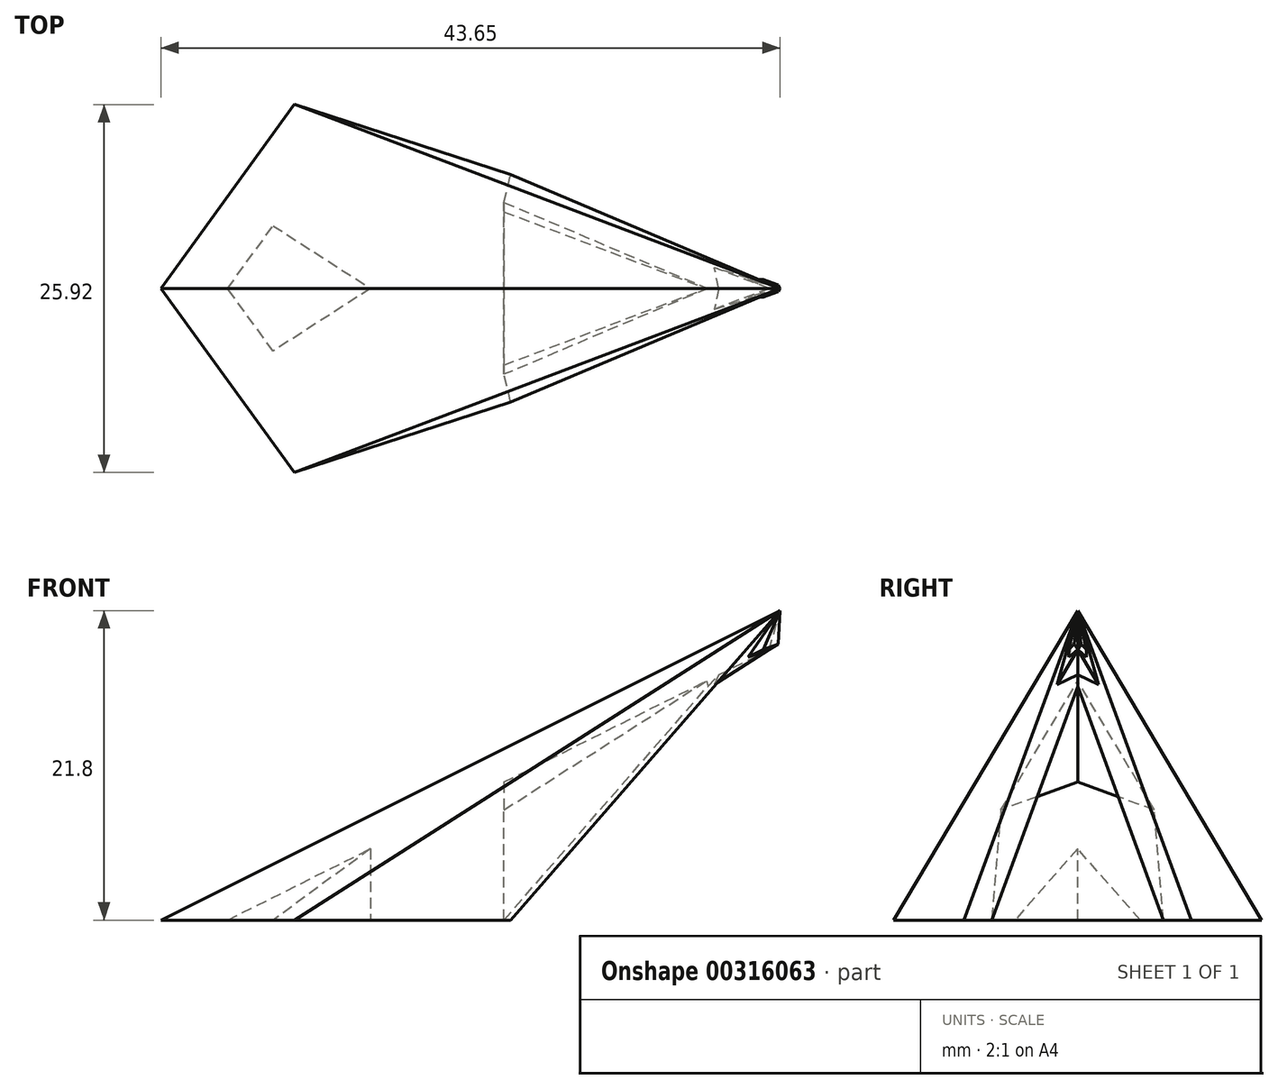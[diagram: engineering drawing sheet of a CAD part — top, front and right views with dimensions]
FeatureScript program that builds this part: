
annotation { "Feature Type Name" : "Feature", "Feature Type Description" : "" }
export const myFeature = defineFeature(function(context is Context, id is Id, definition is map)
    precondition{}
    {
        {
            var Q0;
            Q0=qCreatedBy(makeId("Top.planeOp"),FACE);
            var sketch = newSketch(context, id + "F0", { "sketchPlane" : qUnion([Q0])});
            skCircle(sketch, "E0.cCircle", {"center": v(0, 0) * mm, "radius": 11.03 * mm, "construction": true});
            skLineSegment(sketch, "E0.0", {"start": v(11.03, 8.01) * mm, "end": v(11.03, -8.01) * mm});
            skLineSegment(sketch, "E0.1", {"start": v(11.03, -8.01) * mm, "end": v(-4.21, -12.96) * mm});
            skLineSegment(sketch, "E0.2", {"start": v(-4.21, -12.96) * mm, "end": v(-13.63, 0) * mm});
            skLineSegment(sketch, "E0.3", {"start": v(-13.63, 0) * mm, "end": v(-4.21, 12.96) * mm});
            skLineSegment(sketch, "E0.4", {"start": v(-4.21, 12.96) * mm, "end": v(11.03, 8.01) * mm});
            skPoint(sketch, "E0.0.midPoint", {"position": v(11.03, 0) * mm});
            skSolve(sketch);
        }
        {
            var Q0;
            Q0=qCreatedBy(makeId("Front.planeOp"),FACE);
            var sketch = newSketch(context, id + "F1", { "sketchPlane" : qUnion([Q0])});
            skLineSegment(sketch, "E1", {"start": v(0, 0) * mm, "end": v(30.02, 21.8) * mm});
            skSolve(sketch);
        }
        {
            var Q0;
            Q0=sQuery(id+"F1.wireOp",VERTEX,"E1.end");
            var Q1;
            Q1=sQuery(id+"F0.wireOp",VERTEX,"E0.1.start");
            var Q2;
            Q2=sQuery(id+"F0.wireOp",VERTEX,"E0.2.start");
            cPlane(context, id + "F2", {"entities" : qUnion([Q0, Q1, Q2]), "cplaneType" : CPlaneType.THREE_POINT, "offset" : 25.4 * mm, "oppositeDirection" : true, "width" : 152.4 * mm, "height" : 152.4 * mm});
        }
        {
            var Q0;
            Q0=sQuery(id+"F0.wireOp",VERTEX,"E0.2.start");
            var Q1;
            Q1=sQuery(id+"F0.wireOp",VERTEX,"E0.3.start");
            var Q2;
            Q2=sQuery(id+"F1.wireOp",VERTEX,"E1.end");
            cPlane(context, id + "F3", {"entities" : qUnion([Q0, Q1, Q2]), "cplaneType" : CPlaneType.THREE_POINT, "offset" : 25.4 * mm, "width" : 152.4 * mm, "height" : 152.4 * mm});
        }
        {
            var Q0;
            Q0=sQuery(id+"F1.wireOp",VERTEX,"E1.end");
            var Q1;
            Q1=sQuery(id+"F0.wireOp",VERTEX,"E0.3.start");
            var Q2;
            Q2=sQuery(id+"F0.wireOp",VERTEX,"E0.4.start");
            cPlane(context, id + "F4", {"entities" : qUnion([Q0, Q1, Q2]), "cplaneType" : CPlaneType.THREE_POINT, "offset" : 25.4 * mm, "width" : 152.4 * mm, "height" : 152.4 * mm});
        }
        {
            var Q0;
            Q0=qCreatedBy(id+"F2.planeOp",FACE);
            var sketch = newSketch(context, id + "F5", { "sketchPlane" : qUnion([Q0])});
            skLineSegment(sketch, "E2", {"start": v(28, 21.72) * mm, "end": v(8.03, -0.67) * mm});
            skLineSegment(sketch, "E3", {"start": v(8.03, -0.67) * mm, "end": v(-7.99, -1.1) * mm});
            skLineSegment(sketch, "E4", {"start": v(-7.99, -1.1) * mm, "end": v(28, 21.72) * mm});
            skSolve(sketch);
        }
        {
            var Q0;
            Q0=qCreatedBy(id+"F3.planeOp",FACE);
            var sketch = newSketch(context, id + "F6", { "sketchPlane" : qUnion([Q0])});
            skLineSegment(sketch, "E5", {"start": v(35.88, 7.43) * mm, "end": v(-1.93, -12.19) * mm});
            skLineSegment(sketch, "E6", {"start": v(-1.93, -12.19) * mm, "end": v(-12.34, 0) * mm});
            skLineSegment(sketch, "E7", {"start": v(-12.34, 0) * mm, "end": v(35.88, 7.43) * mm});
            skSolve(sketch);
        }
        {
            var Q0;
            Q0=qCreatedBy(id+"F4.planeOp",FACE);
            var sketch = newSketch(context, id + "F7", { "sketchPlane" : qUnion([Q0])});
            skLineSegment(sketch, "E8", {"start": v(-1.93, 12.19) * mm, "end": v(-12.34, 0) * mm});
            skLineSegment(sketch, "E9", {"start": v(-12.34, 0) * mm, "end": v(35.88, -7.43) * mm});
            skLineSegment(sketch, "E10", {"start": v(35.88, -7.43) * mm, "end": v(-1.93, 12.19) * mm});
            skSolve(sketch);
        }
        {
            var Q0;
            Q0=sQuery(id+"F0.wireOp",VERTEX,"E0.4.end");
            var Q1;
            Q1=sQuery(id+"F5.wireOp",VERTEX,"E4.end");
            var Q2;
            Q2=sQuery(id+"F7.wireOp",VERTEX,"E10.end");
            cPlane(context, id + "F8", {"entities" : qUnion([Q0, Q1, Q2]), "cplaneType" : CPlaneType.THREE_POINT, "offset" : 25.4 * mm, "width" : 152.4 * mm, "height" : 152.4 * mm});
        }
        {
            var Q0;
            Q0=qCreatedBy(id+"F8.planeOp",FACE);
            var sketch = newSketch(context, id + "F9", { "sketchPlane" : qUnion([Q0])});
            skLineSegment(sketch, "E11", {"start": v(-28, 21.72) * mm, "end": v(7.99, -1.1) * mm});
            skLineSegment(sketch, "E12", {"start": v(7.99, -1.1) * mm, "end": v(-8.03, -0.67) * mm});
            skLineSegment(sketch, "E13", {"start": v(-8.03, -0.67) * mm, "end": v(-28, 21.72) * mm});
            skSolve(sketch);
        }
        {
            var Q0;
            Q0=makeQuery(id+"F9.imprint","IMPRINT",FACE,{"disambiguationData":[TD([[makeQuery(id+"F9.imprint","IMPRINT",EDGE,{"derivedFrom":sQuery(id+"F9.wireOp",EDGE,"E11")}),-1.0]])]});
            extrude(context, id + "F10", {"entities" : qUnion([Q0]), "oppositeDirection" : true, "depth" : 2 * mm});
        }
        {
            var Q0;
            Q0=makeQuery(id+"F7.imprint","IMPRINT",FACE,{"disambiguationData":[TD([[makeQuery(id+"F7.imprint","IMPRINT",EDGE,{"derivedFrom":sQuery(id+"F7.wireOp",EDGE,"E8")}),1.0]])]});
            extrude(context, id + "F11", {"entities" : qUnion([Q0]), "operationType" : NewBodyOperationType.ADD, "oppositeDirection" : true, "depth" : 2 * mm});
        }
        {
            var Q0;
            Q0=makeQuery(id+"F6.imprint","IMPRINT",FACE,{"disambiguationData":[TD([[makeQuery(id+"F6.imprint","IMPRINT",EDGE,{"derivedFrom":sQuery(id+"F6.wireOp",EDGE,"E5")}),-1.0]])]});
            extrude(context, id + "F12", {"entities" : qUnion([Q0]), "operationType" : NewBodyOperationType.ADD, "oppositeDirection" : true, "depth" : 2 * mm});
        }
        {
            var Q0;
            Q0=makeQuery(id+"F5.imprint","IMPRINT",FACE,{"disambiguationData":[TD([[makeQuery(id+"F5.imprint","IMPRINT",EDGE,{"derivedFrom":sQuery(id+"F5.wireOp",EDGE,"E2")}),-1.0]])]});
            extrude(context, id + "F13", {"entities" : qUnion([Q0]), "operationType" : NewBodyOperationType.ADD, "oppositeDirection" : true, "depth" : 2 * mm});
        }
        {
            var Q0;
            Q0=makeQuery(id+"F13.opExtrude","CAP_FACE",FACE,{"disambiguationData":[OSD([sQuery(id+"F5.wireOp",EDGE,"E2"),sQuery(id+"F5.wireOp",EDGE,"E3"),sQuery(id+"F5.wireOp",EDGE,"E4")])],"isStart":true});
            var sketch = newSketch(context, id + "F14", { "sketchPlane" : qUnion([Q0])});
            skLineSegment(sketch, "E14.bottom", {"start": v(21.55, 22.32) * mm, "end": v(30.03, 22.32) * mm});
            skLineSegment(sketch, "E14.top", {"start": v(21.55, 16.8) * mm, "end": v(30.03, 16.8) * mm});
            skLineSegment(sketch, "E14.left", {"start": v(21.55, 22.32) * mm, "end": v(21.55, 16.8) * mm});
            skLineSegment(sketch, "E14.right", {"start": v(30.03, 22.32) * mm, "end": v(30.03, 16.8) * mm});
            skSolve(sketch);
        }
        {
            var Q0;
            Q0=qSketchRegion(id+"F14",true);
            extrude(context, id + "F15", {"entities" : qUnion([Q0]), "operationType" : NewBodyOperationType.REMOVE, "depth" : 25.4 * mm});
        }
        {
            var Q0;
            Q0=makeQuery(id+"F11.opExtrude","CAP_FACE",FACE,{"disambiguationData":[OSD([sQuery(id+"F7.wireOp",EDGE,"E8"),sQuery(id+"F7.wireOp",EDGE,"E9"),sQuery(id+"F7.wireOp",EDGE,"E10")])],"isStart":true});
            var sketch = newSketch(context, id + "F16", { "sketchPlane" : qUnion([Q0])});
            skLineSegment(sketch, "E15.bottom", {"start": v(43.57, -4.34) * mm, "end": v(21.34, -4.34) * mm});
            skLineSegment(sketch, "E15.top", {"start": v(43.57, -8.99) * mm, "end": v(21.34, -8.99) * mm});
            skLineSegment(sketch, "E15.left", {"start": v(43.57, -4.34) * mm, "end": v(43.57, -8.99) * mm});
            skLineSegment(sketch, "E15.right", {"start": v(21.34, -4.34) * mm, "end": v(21.34, -8.99) * mm});
            skSolve(sketch);
        }
        {
            var Q0;
            Q0=qSketchRegion(id+"F16",true);
            extrude(context, id + "F17", {"entities" : qUnion([Q0]), "operationType" : NewBodyOperationType.REMOVE, "depth" : 25.4 * mm});
        }
        {
            var Q0;
            Q0=makeQuery(id+"F12.opExtrude","CAP_FACE",FACE,{"disambiguationData":[OSD([sQuery(id+"F6.wireOp",EDGE,"E5"),sQuery(id+"F6.wireOp",EDGE,"E6"),sQuery(id+"F6.wireOp",EDGE,"E7")])],"isStart":true});
            var sketch = newSketch(context, id + "F18", { "sketchPlane" : qUnion([Q0])});
            skLineSegment(sketch, "E16.bottom", {"start": v(31.54, 2.1) * mm, "end": v(39.49, 2.1) * mm});
            skLineSegment(sketch, "E16.top", {"start": v(31.54, 9.38) * mm, "end": v(39.49, 9.38) * mm});
            skLineSegment(sketch, "E16.left", {"start": v(31.54, 2.1) * mm, "end": v(31.54, 9.38) * mm});
            skLineSegment(sketch, "E16.right", {"start": v(39.49, 2.1) * mm, "end": v(39.49, 9.38) * mm});
            skSolve(sketch);
        }
        {
            var Q0;
            Q0=qSketchRegion(id+"F18",true);
            extrude(context, id + "F19", {"entities" : qUnion([Q0]), "operationType" : NewBodyOperationType.REMOVE, "depth" : 25.4 * mm});
        }
        {
            var Q0;
            Q0=makeQuery(id+"F10.opExtrude","CAP_FACE",FACE,{"disambiguationData":[OSD([sQuery(id+"F9.wireOp",EDGE,"E11"),sQuery(id+"F9.wireOp",EDGE,"E12"),sQuery(id+"F9.wireOp",EDGE,"E13")])],"isStart":true});
            var sketch = newSketch(context, id + "F20", { "sketchPlane" : qUnion([Q0])});
            skLineSegment(sketch, "E17.bottom", {"start": v(-23.79, 12.88) * mm, "end": v(-29.7, 12.88) * mm});
            skLineSegment(sketch, "E17.top", {"start": v(-23.79, 24.27) * mm, "end": v(-29.7, 24.27) * mm});
            skLineSegment(sketch, "E17.left", {"start": v(-23.79, 12.88) * mm, "end": v(-23.79, 24.27) * mm});
            skLineSegment(sketch, "E17.right", {"start": v(-29.7, 12.88) * mm, "end": v(-29.7, 24.27) * mm});
            skSolve(sketch);
        }
        {
            var Q0;
            Q0=qSketchRegion(id+"F20",true);
            extrude(context, id + "F21", {"entities" : qUnion([Q0]), "operationType" : NewBodyOperationType.REMOVE, "depth" : 25.4 * mm});
        }
        {
            var Q0;
            Q0=qSketchRegion(id+"F0",true);
            extrude(context, id + "F22", {"entities" : qUnion([Q0]), "operationType" : NewBodyOperationType.REMOVE, "oppositeDirection" : true, "depth" : 25.4 * mm});
        }
        {
            var Q0;
            Q0=makeQuery(id+"F22.boolean.opBoolean","COPY",FACE,{"derivedFrom":makeQuery(id+"F22.opExtrude","CAP_FACE",FACE,{"disambiguationData":[OSD([sQuery(id+"F0.wireOp",EDGE,"E0.0"),sQuery(id+"F0.wireOp",EDGE,"E0.1"),sQuery(id+"F0.wireOp",EDGE,"E0.2"),sQuery(id+"F0.wireOp",EDGE,"E0.3"),sQuery(id+"F0.wireOp",EDGE,"E0.4")])],"isStart":true})});
            var sketch = newSketch(context, id + "F23", { "sketchPlane" : qUnion([Q0])});
            skLineSegment(sketch, "E18", {"start": v(-8.92, 6.48) * mm, "end": v(10.55, -6.06) * mm});
            skLineSegment(sketch, "E19", {"start": v(10.55, 6.06) * mm, "end": v(-8.92, -6.48) * mm});
            skLineSegment(sketch, "E20", {"start": v(10.55, 6.06) * mm, "end": v(10.55, -6.06) * mm});
            skLineSegment(sketch, "E21", {"start": v(6.73, 7.3) * mm, "end": v(6.73, -7.3) * mm});
            skSolve(sketch);
        }
        {
            var Q0;
            {var subQ12=sQuery(id+"F23.wireOp",EDGE,"E19");var subQ16=sQuery(id+"F23.wireOp",EDGE,"E18");var subQ18=makeQuery(id+"F23.imprint","INTERSECT",VERTEX,{"derivedFrom":[subQ16,subQ12]});Q0=makeQuery(id+"F23.imprint","IMPRINT",FACE,{"disambiguationData":[TD([[makeQuery(id+"F23.imprint","IMPRINT",EDGE,{"disambiguationData":[TD([[subQ18,-1.0]])],"derivedFrom":subQ16}),-1.0]])]});}
            var Q1;
            {var subQ17=sQuery(id+"F23.wireOp",EDGE,"E19");var subQ24=sQuery(id+"F23.wireOp",EDGE,"E18");var subQ26=makeQuery(id+"F23.imprint","INTERSECT",VERTEX,{"derivedFrom":[subQ24,subQ17]});Q1=makeQuery(id+"F23.imprint","IMPRINT",FACE,{"disambiguationData":[TD([[makeQuery(id+"F23.imprint","IMPRINT",EDGE,{"disambiguationData":[TD([[subQ26,1.0]])],"derivedFrom":subQ17}),-1.0]])]});}
            var Q2;
            {var subQ0=sQuery(id+"F23.wireOp",EDGE,"E19");var subQ1=sQuery(id+"F23.wireOp",EDGE,"E18");var subQ2=makeQuery(id+"F23.imprint","INTERSECT",VERTEX,{"derivedFrom":[subQ1,subQ0]});Q2=makeQuery(id+"F23.imprint","IMPRINT",FACE,{"disambiguationData":[TD([[makeQuery(id+"F23.imprint","IMPRINT",EDGE,{"disambiguationData":[TD([[subQ2,-1.0]])],"derivedFrom":subQ1}),1.0]])]});}
            var Q3;
            {var subQ0=sQuery(id+"F23.wireOp",EDGE,"E19");var subQ23=sQuery(id+"F23.wireOp",EDGE,"E21");var subQ24=makeQuery(id+"F23.imprint","INTERSECT",VERTEX,{"derivedFrom":[subQ0,subQ23]});Q3=makeQuery(id+"F23.imprint","IMPRINT",FACE,{"disambiguationData":[TD([[makeQuery(id+"F23.imprint","IMPRINT",EDGE,{"disambiguationData":[TD([[subQ24,1.0]])],"derivedFrom":subQ23}),1.0]])]});}
            var Q4;
            {var subQ0=sQuery(id+"F23.wireOp",EDGE,"E20");Q4=makeQuery(id+"F23.imprint","IMPRINT",FACE,{"disambiguationData":[TD([[makeQuery(id+"F23.imprint","IMPRINT",EDGE,{"derivedFrom":subQ0}),-1.0]])]});}
            var Q5;
            {var subQ0=sQuery(id+"F23.wireOp",EDGE,"E18");var subQ14=sQuery(id+"F23.wireOp",EDGE,"E21");var subQ15=makeQuery(id+"F23.imprint","INTERSECT",VERTEX,{"derivedFrom":[subQ0,subQ14]});Q5=makeQuery(id+"F23.imprint","IMPRINT",FACE,{"disambiguationData":[TD([[makeQuery(id+"F23.imprint","IMPRINT",EDGE,{"disambiguationData":[TD([[subQ15,-1.0]])],"derivedFrom":subQ14}),1.0]])]});}
            extrude(context, id + "F24", {"entities" : qUnion([Q0, Q1, Q2, Q3, Q4, Q5]), "operationType" : NewBodyOperationType.ADD, "oppositeDirection" : true, "depth" : 10 * mm});
        }
        {
            var Q0;
            Q0=makeQuery(id+"F17.boolean.opBoolean","MERGE",FACE,{"derivedFrom":[makeQuery(id+"F11.opExtrude","CAP_FACE",FACE,{"disambiguationData":[OSD([sQuery(id+"F7.wireOp",EDGE,"E8"),sQuery(id+"F7.wireOp",EDGE,"E9"),sQuery(id+"F7.wireOp",EDGE,"E10")])],"isStart":true}),makeQuery(id+"F17.opExtrude","CAP_FACE",FACE,{"disambiguationData":[OSD([sQuery(id+"F16.wireOp",EDGE,"E15.bottom"),sQuery(id+"F16.wireOp",EDGE,"E15.top"),sQuery(id+"F16.wireOp",EDGE,"E15.left"),sQuery(id+"F16.wireOp",EDGE,"E15.right")])],"isStart":true})]});
            var sketch = newSketch(context, id + "F25", { "sketchPlane" : qUnion([Q0])});
            skLineSegment(sketch, "E22.bottom", {"start": v(36.55, 15.1) * mm, "end": v(-21.23, 15.1) * mm});
            skLineSegment(sketch, "E22.top", {"start": v(36.55, -15.44) * mm, "end": v(-21.23, -15.44) * mm});
            skLineSegment(sketch, "E22.left", {"start": v(36.55, 15.1) * mm, "end": v(36.55, -15.44) * mm});
            skLineSegment(sketch, "E22.right", {"start": v(-21.23, 15.1) * mm, "end": v(-21.23, -15.44) * mm});
            skSolve(sketch);
        }
        {
            var Q0;
            Q0 = qSketchRegion(id + "F25", true);
            extrude(context, id + "F26", {"entities" : qUnion([Q0]), "operationType" : NewBodyOperationType.REMOVE, "depth" : 25.4 * mm});
        }
        {
            var Q0;
            Q0=makeQuery(id+"F19.boolean.opBoolean","MERGE",FACE,{"derivedFrom":[makeQuery(id+"F12.opExtrude","CAP_FACE",FACE,{"disambiguationData":[OSD([sQuery(id+"F6.wireOp",EDGE,"E5"),sQuery(id+"F6.wireOp",EDGE,"E6"),sQuery(id+"F6.wireOp",EDGE,"E7")])],"isStart":true}),makeQuery(id+"F19.opExtrude","CAP_FACE",FACE,{"disambiguationData":[OSD([sQuery(id+"F18.wireOp",EDGE,"E16.bottom"),sQuery(id+"F18.wireOp",EDGE,"E16.top"),sQuery(id+"F18.wireOp",EDGE,"E16.left"),sQuery(id+"F18.wireOp",EDGE,"E16.right")])],"isStart":true})]});
            var sketch = newSketch(context, id + "F27", { "sketchPlane" : qUnion([Q0])});
            skLineSegment(sketch, "E23.bottom", {"start": v(25.49, -15.31) * mm, "end": v(-13.85, -15.31) * mm});
            skLineSegment(sketch, "E23.top", {"start": v(25.49, 6.27) * mm, "end": v(-13.85, 6.27) * mm});
            skLineSegment(sketch, "E23.left", {"start": v(25.49, -15.31) * mm, "end": v(25.49, 6.27) * mm});
            skLineSegment(sketch, "E23.right", {"start": v(-13.85, -15.31) * mm, "end": v(-13.85, 6.27) * mm});
            skSolve(sketch);
        }
        {
            var Q0;
            Q0 = qSketchRegion(id + "F27", true);
            extrude(context, id + "F28", {"entities" : qUnion([Q0]), "operationType" : NewBodyOperationType.REMOVE, "depth" : 25.4 * mm});
        }
    });
